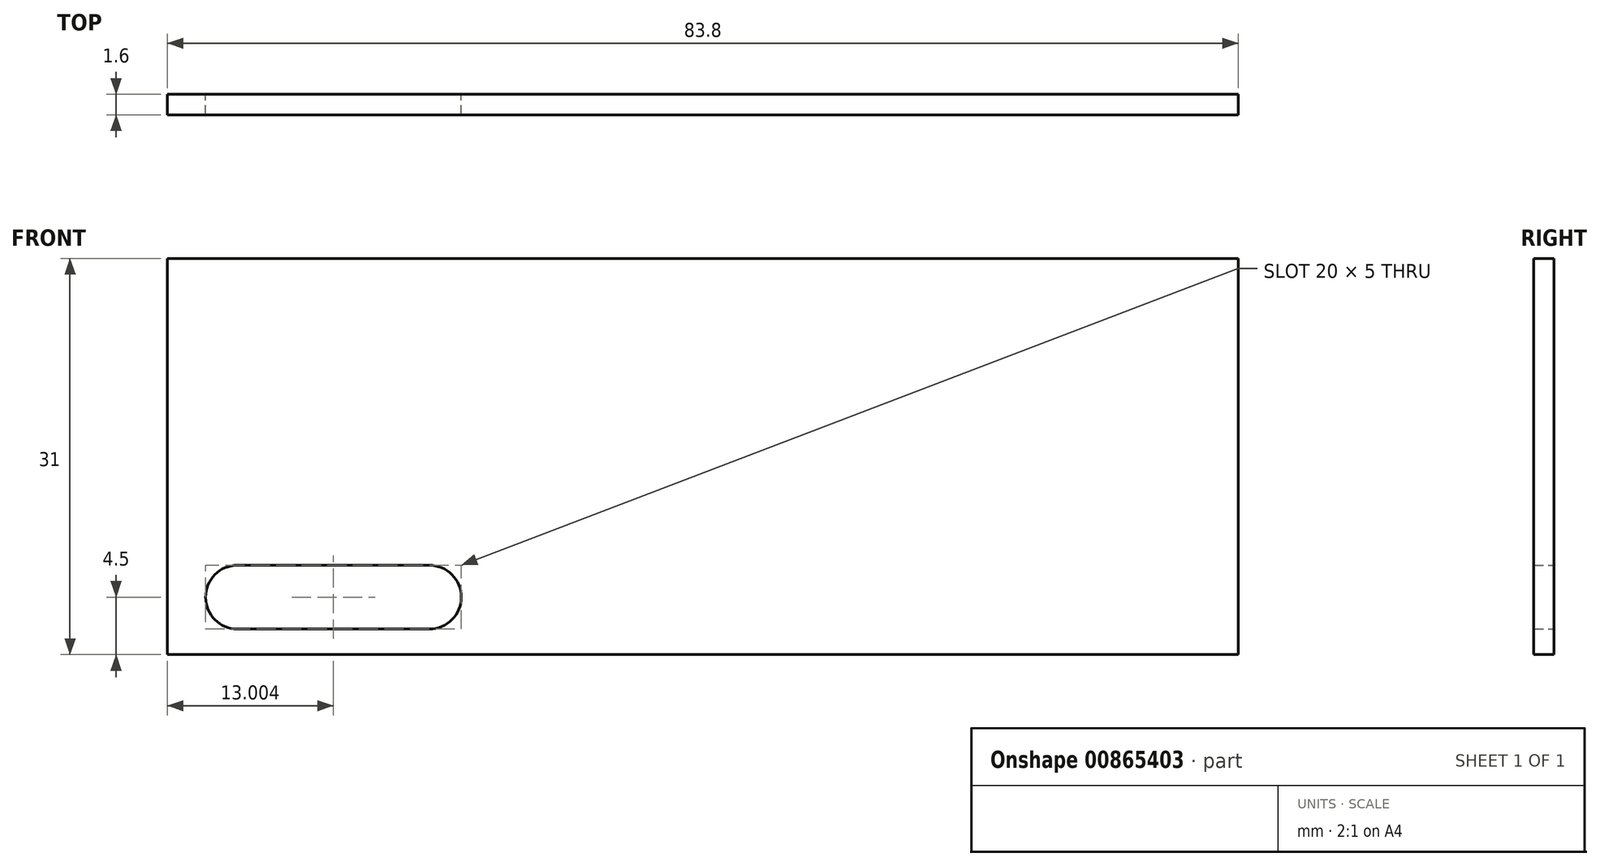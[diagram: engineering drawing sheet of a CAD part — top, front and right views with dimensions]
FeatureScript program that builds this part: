
annotation { "Feature Type Name" : "Feature", "Feature Type Description" : "" }
export const myFeature = defineFeature(function(context is Context, id is Id, definition is map)
    precondition{}
    {
        {
            var Q0;
            Q0=qCreatedBy(makeId("Front.planeOp"),FACE);
            var sketch = newSketch(context, id + "F0", { "sketchPlane" : qUnion([Q0])});
            skLineSegment(sketch, "E0.bottom", {"start": v(-40.25, 15.5) * mm, "end": v(43.55, 15.5) * mm});
            skLineSegment(sketch, "E0.top", {"start": v(-40.25, -15.5) * mm, "end": v(43.55, -15.5) * mm});
            skLineSegment(sketch, "E0.left", {"start": v(-40.25, 15.5) * mm, "end": v(-40.25, -15.5) * mm});
            skLineSegment(sketch, "E0.right", {"start": v(43.55, 15.5) * mm, "end": v(43.55, -15.5) * mm});
            skLineSegment(sketch, "E1", {"start": v(-34.75, -8.5) * mm, "end": v(-19.75, -8.5) * mm});
            skLineSegment(sketch, "E2", {"start": v(-34.75, -13.5) * mm, "end": v(-19.75, -13.5) * mm});
            skArc(sketch, "E3", {"start": v(-34.75, -8.5) * mm, "mid": v(-37.25, -11) * mm, "end": v(-34.75, -13.5) * mm});
            skArc(sketch, "E4", {"start": v(-19.75, -13.5) * mm, "mid": v(-17.25, -11) * mm, "end": v(-19.75, -8.5) * mm});
            skSolve(sketch);
        }
        {
            var Q0;
            Q0=makeQuery(id+"F0.imprint","IMPRINT",FACE,{"disambiguationData":[TD([[makeQuery(id+"F0.imprint","IMPRINT",EDGE,{"derivedFrom":sQuery(id+"F0.wireOp",EDGE,"E0.bottom")}),-1.0]])]});
            extrude(context, id + "F1", {"entities" : qUnion([Q0]), "depth" : 1.6 * mm, "offsetDistance" : 25 * mm});
        }
    });
